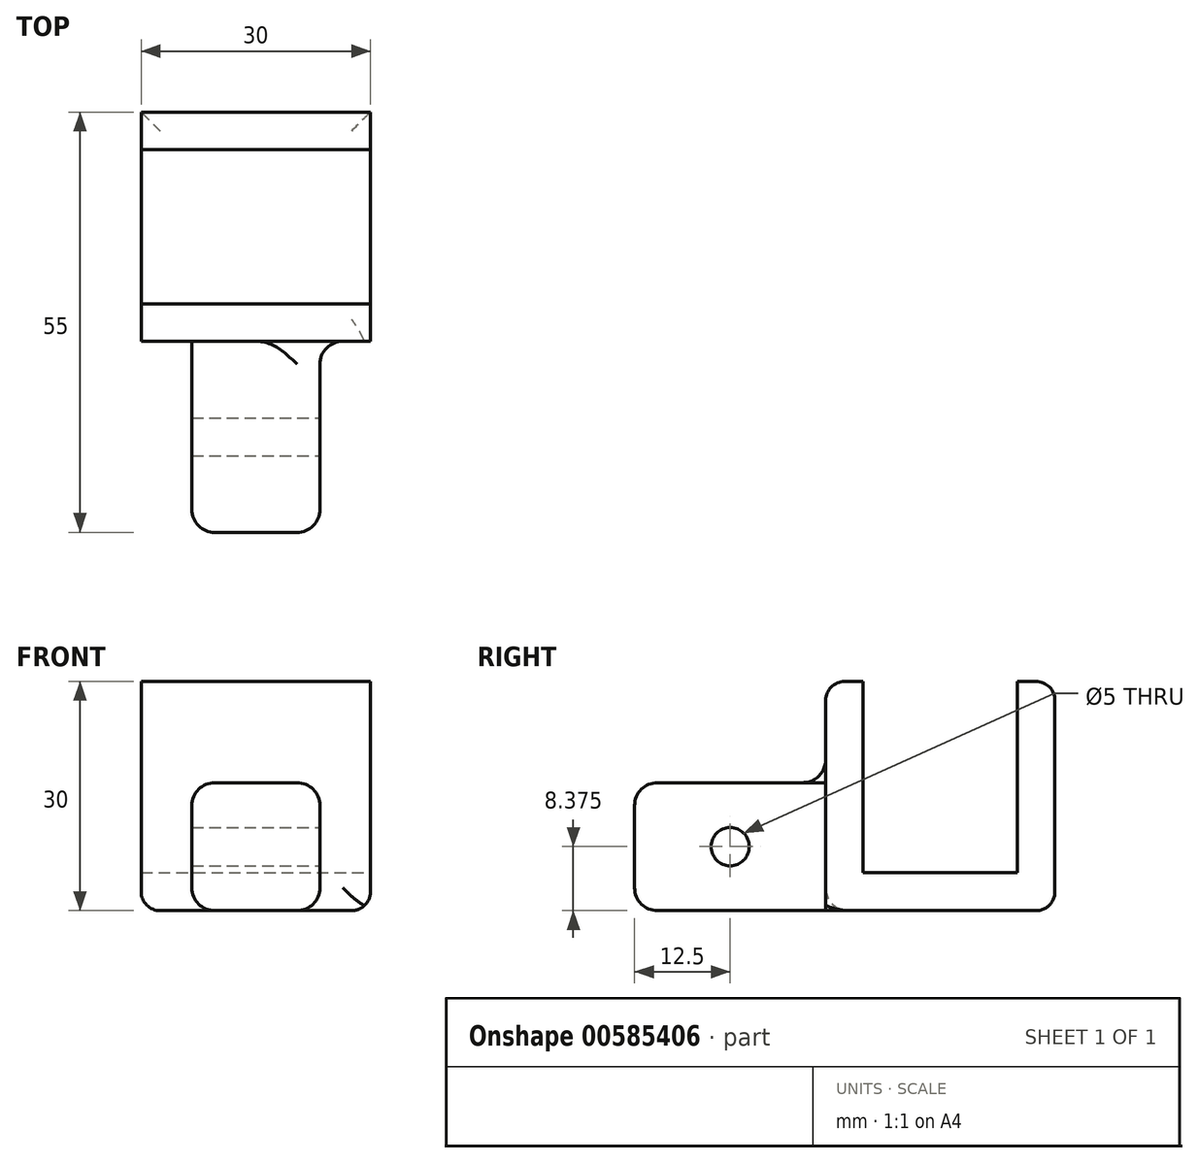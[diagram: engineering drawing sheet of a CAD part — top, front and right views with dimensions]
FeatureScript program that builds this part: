
annotation { "Feature Type Name" : "Feature", "Feature Type Description" : "" }
export const myFeature = defineFeature(function(context is Context, id is Id, definition is map)
    precondition{}
    {
        {
            var Q0;
            Q0=qCreatedBy(makeId("Top.planeOp"),FACE);
            var sketch = newSketch(context, id + "F0", { "sketchPlane" : qUnion([Q0])});
            skLineSegment(sketch, "E0.bottom", {"start": v(0, 0) * mm, "end": v(30, 0) * mm});
            skLineSegment(sketch, "E0.top", {"start": v(0, 30) * mm, "end": v(30, 30) * mm});
            skLineSegment(sketch, "E0.left", {"start": v(0, 0) * mm, "end": v(0, 30) * mm});
            skLineSegment(sketch, "E0.right", {"start": v(30, 0) * mm, "end": v(30, 30) * mm});
            skSolve(sketch);
        }
        {
            var Q0;
            Q0=makeQuery(id+"F0.imprint","IMPRINT",FACE,{"disambiguationData":[TD([[makeQuery(id+"F0.imprint","IMPRINT",EDGE,{"derivedFrom":sQuery(id+"F0.wireOp",EDGE,"E0.bottom")}),1.0]])]});
            extrude(context, id + "F1", {"entities" : qUnion([Q0]), "depth" : 5 * mm, "offsetDistance" : 25 * mm});
        }
        {
            var Q0;
            Q0=makeQuery(id+"F1.opExtrude","CAP_FACE",FACE,{"disambiguationData":[OSD([sQuery(id+"F0.wireOp",EDGE,"E0.bottom"),sQuery(id+"F0.wireOp",EDGE,"E0.top"),sQuery(id+"F0.wireOp",EDGE,"E0.left"),sQuery(id+"F0.wireOp",EDGE,"E0.right")])],"isStart":false});
            var sketch = newSketch(context, id + "F2", { "sketchPlane" : qUnion([Q0])});
            skLineSegment(sketch, "E1.bottom", {"start": v(0, 30) * mm, "end": v(30, 30) * mm});
            skLineSegment(sketch, "E1.top", {"start": v(0, 25.1) * mm, "end": v(30, 25.1) * mm});
            skLineSegment(sketch, "E1.left", {"start": v(0, 30) * mm, "end": v(0, 25.1) * mm});
            skLineSegment(sketch, "E1.right", {"start": v(30, 30) * mm, "end": v(30, 25.1) * mm});
            skLineSegment(sketch, "E2", {"start": v(0, 15) * mm, "end": v(30, 15) * mm, "construction": true});
            skLineSegment(sketch, "E3.MirrorCS", {"start": v(0, 0) * mm, "end": v(30, 0) * mm});
            skLineSegment(sketch, "E4.MirrorCS", {"start": v(0, 4.9) * mm, "end": v(30, 4.9) * mm});
            skLineSegment(sketch, "E5.MirrorCS", {"start": v(0, 0) * mm, "end": v(0, 4.9) * mm});
            skLineSegment(sketch, "E6.MirrorCS", {"start": v(30, 0) * mm, "end": v(30, 4.9) * mm});
            skSolve(sketch);
        }
        {
            var Q0;
            Q0=makeQuery(id+"F2.imprint","IMPRINT",FACE,{"disambiguationData":[TD([[makeQuery(id+"F2.imprint","IMPRINT",EDGE,{"derivedFrom":sQuery(id+"F2.wireOp",EDGE,"E1.bottom")}),-1.0]])]});
            var Q1;
            Q1=makeQuery(id+"F2.imprint","IMPRINT",FACE,{"disambiguationData":[TD([[makeQuery(id+"F2.imprint","IMPRINT",EDGE,{"derivedFrom":sQuery(id+"F2.wireOp",EDGE,"E3.MirrorCS")}),1.0]])]});
            extrude(context, id + "F3", {"entities" : qUnion([Q0, Q1]), "operationType" : NewBodyOperationType.ADD, "depth" : 25 * mm, "offsetDistance" : 25 * mm});
        }
        {
            var Q0;
            Q0=makeQuery(id+"F3.boolean.opBoolean","MERGE",FACE,{"derivedFrom":[makeQuery(id+"F1.opExtrude","SWEPT_FACE",FACE,{"disambiguationData":[OSD([sQuery(id+"F0.wireOp",EDGE,"E0.bottom")])]}),makeQuery(id+"F3.opExtrude","SWEPT_FACE",FACE,{"disambiguationData":[OSD([sQuery(id+"F2.wireOp",EDGE,"E3.MirrorCS")])]})]});
            var sketch = newSketch(context, id + "F4", { "sketchPlane" : qUnion([Q0])});
            skLineSegment(sketch, "E7", {"start": v(15, 0) * mm, "end": v(15, 30) * mm, "construction": true});
            skLineSegment(sketch, "E8.right", {"start": v(23.38, 0) * mm, "end": v(23.38, 16.75) * mm});
            skLineSegment(sketch, "E9.MirrorCS", {"start": v(6.63, 0) * mm, "end": v(6.63, 16.75) * mm});
            skLineSegment(sketch, "E10", {"start": v(6.63, 0) * mm, "end": v(23.38, 0) * mm});
            skLineSegment(sketch, "E11", {"start": v(6.63, 16.75) * mm, "end": v(23.38, 16.75) * mm});
            skSolve(sketch);
        }
        {
            var Q0;
            Q0=makeQuery(id+"F4.imprint","IMPRINT",FACE,{"disambiguationData":[TD([[makeQuery(id+"F4.imprint","IMPRINT",EDGE,{"derivedFrom":sQuery(id+"F4.wireOp",EDGE,"E8.right")}),1.0]])]});
            extrude(context, id + "F5", {"entities" : qUnion([Q0]), "operationType" : NewBodyOperationType.ADD, "depth" : 25 * mm, "offsetDistance" : 25 * mm});
        }
        {
            var Q0;
            Q0=makeQuery(id+"F5.opExtrude","CAP_EDGE",EDGE,{"disambiguationData":[OSD([sQuery(id+"F4.wireOp",EDGE,"E8.top"),sQuery(id+"F4.wireOp",EDGE,"2b287bc2-b91f-4d5c-92d6-7b527b62b60b0.MirrorCS")])],"isStart":true});
            var Q1;
            Q1=makeQuery(id+"F5.opExtrude","CAP_EDGE",EDGE,{"disambiguationData":[OSD([sQuery(id+"F4.wireOp",EDGE,"E8.top"),sQuery(id+"F4.wireOp",EDGE,"2b287bc2-b91f-4d5c-92d6-7b527b62b60b0.MirrorCS")])],"isStart":false});
            var Q2;
            Q2=makeQuery(id+"F5.opExtrude","CAP_EDGE",EDGE,{"disambiguationData":[OSD([sQuery(id+"F4.wireOp",EDGE,"E9.MirrorCS")])],"isStart":false});
            var Q3;
            Q3=makeQuery(id+"F5.opExtrude","SWEPT_EDGE",EDGE,{"disambiguationData":[OSD([sQuery(id+"F4.wireOp",EDGE,"2b287bc2-b91f-4d5c-92d6-7b527b62b60b0.MirrorCS"),sQuery(id+"F4.wireOp",EDGE,"E9.MirrorCS")])]});
            var Q4;
            Q4=makeQuery(id+"F5.opExtrude","SWEPT_EDGE",EDGE,{"disambiguationData":[OSD([sQuery(id+"F0.wireOp",EDGE,"E0.bottom"),sQuery(id+"F4.wireOp",EDGE,"6c4bcf0f-9b09-45c1-b559-46fb84961e650.MirrorCS"),sQuery(id+"F4.wireOp",EDGE,"E9.MirrorCS")])]});
            var Q5;
            Q5=makeQuery(id+"F5.opExtrude","CAP_EDGE",EDGE,{"disambiguationData":[OSD([sQuery(id+"F4.wireOp",EDGE,"E8.right")])],"isStart":true});
            var Q6;
            Q6=makeQuery(id+"F5.opExtrude","SWEPT_FACE",FACE,{"disambiguationData":[OSD([sQuery(id+"F4.wireOp",EDGE,"E8.right")])]});
            var Q7;
            Q7=makeQuery(id+"F5.opExtrude","CAP_EDGE",EDGE,{"disambiguationData":[OSD([sQuery(id+"F4.wireOp",EDGE,"E8.bottom"),sQuery(id+"F4.wireOp",EDGE,"6c4bcf0f-9b09-45c1-b559-46fb84961e650.MirrorCS")])],"isStart":false});
            fillet(context, id + "F6", {"entities" : qUnion([Q0, Q1, Q2, Q3, Q4, Q5, Q6, Q7]), "radius" : 3 * mm, "tangentPropagation" : true, "allowEdgeOverflow" : false});
        }
        {
            var Q0;
            Q0=makeQuery(id+"F3.opExtrude","CAP_EDGE",EDGE,{"disambiguationData":[OSD([sQuery(id+"F2.wireOp",EDGE,"E1.bottom")])],"isStart":false});
            var Q1;
            Q1=makeQuery(id+"F3.opExtrude","CAP_EDGE",EDGE,{"disambiguationData":[OSD([sQuery(id+"F2.wireOp",EDGE,"E3.MirrorCS")])],"isStart":false});
            var Q2;
            Q2=makeQuery(id+"F1.opExtrude","CAP_EDGE",EDGE,{"disambiguationData":[OSD([sQuery(id+"F0.wireOp",EDGE,"E0.top")])],"isStart":true});
            var Q3;
            Q3=makeQuery(id+"F1.opExtrude","CAP_EDGE",EDGE,{"disambiguationData":[OSD([sQuery(id+"F0.wireOp",EDGE,"E0.right")])],"isStart":true});
            var Q4;
            Q4=makeQuery(id+"F1.opExtrude","CAP_EDGE",EDGE,{"disambiguationData":[OSD([sQuery(id+"F0.wireOp",EDGE,"E0.left")])],"isStart":true});
            fillet(context, id + "F7", {"entities" : qUnion([Q0, Q1, Q2, Q3, Q4]), "radius" : 2.5 * mm, "tangentPropagation" : true, "allowEdgeOverflow" : false});
        }
        {
            var Q0;
            Q0=makeQuery(id+"F5.opExtrude","CAP_EDGE",EDGE,{"disambiguationData":[OSD([sQuery(id+"F4.wireOp",EDGE,"E11")])],"isStart":false});
            var Q1;
            Q1=makeQuery(id+"F5.opExtrude","CAP_EDGE",EDGE,{"disambiguationData":[OSD([sQuery(id+"F4.wireOp",EDGE,"E10")])],"isStart":false});
            fillet(context, id + "F8", {"entities" : qUnion([Q0, Q1]), "radius" : 3 * mm, "tangentPropagation" : true, "allowEdgeOverflow" : false});
        }
        {
            var Q0;
            Q0=makeQuery(id+"F5.opExtrude","SWEPT_FACE",FACE,{"disambiguationData":[OSD([sQuery(id+"F4.wireOp",EDGE,"E8.right")])]});
            var sketch = newSketch(context, id + "F9", { "sketchPlane" : qUnion([Q0])});
            skLineSegment(sketch, "E12", {"start": v(-22, 13.75) * mm, "end": v(-3, 3) * mm, "construction": true});
            skLineSegment(sketch, "E13", {"start": v(-3, 13.75) * mm, "end": v(-22, 3) * mm, "construction": true});
            skCircle(sketch, "E14", {"center": v(-12.5, 8.37) * mm, "radius": 2.5 * mm});
            skSolve(sketch);
        }
        {
            var Q0;
            Q0=makeQuery(id+"F9.imprint","IMPRINT",FACE,{"disambiguationData":[TD([[makeQuery(id+"F9.imprint","IMPRINT",EDGE,{"derivedFrom":sQuery(id+"F9.wireOp",EDGE,"E14")}),1.0]])]});
            extrude(context, id + "F10", {"entities" : qUnion([Q0]), "operationType" : NewBodyOperationType.REMOVE, "endBound" : BoundingType.UP_TO_NEXT, "oppositeDirection" : true, "depth" : 25 * mm, "offsetDistance" : 25 * mm});
        }
    });
